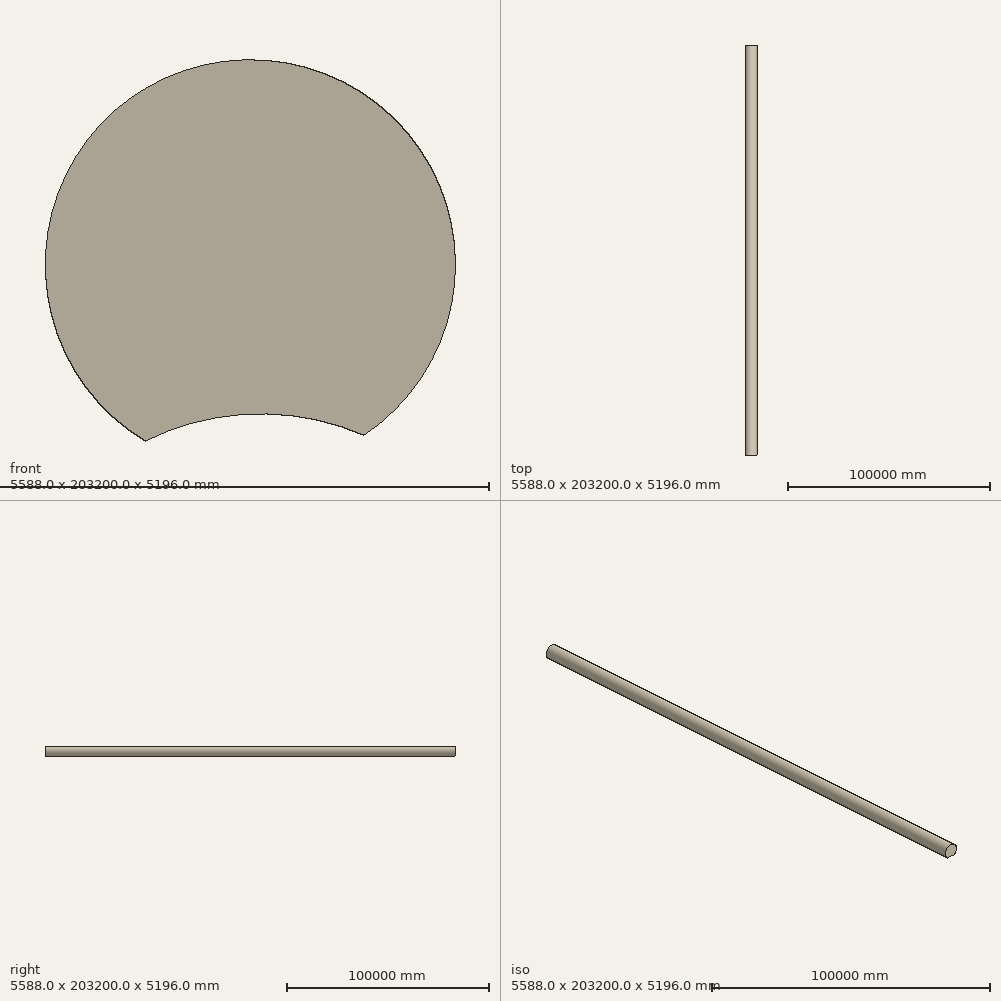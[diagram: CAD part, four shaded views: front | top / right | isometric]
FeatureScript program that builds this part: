
annotation { "Feature Type Name" : "Feature", "Feature Type Description" : "" }
export const myFeature = defineFeature(function(context is Context, id is Id, definition is map)
    precondition{}
    {
        {
            var Q0;
            Q0=qCreatedBy(makeId("Front.planeOp"),FACE);
            var sketch = newSketch(context, id + "F0", { "sketchPlane" : qUnion([Q0])});
            skArc(sketch, "E0", {"start": v(1550.8, -2324.1) * mm, "mid": v(-73.07, 2793.04) * mm, "end": v(-1427.15, -2402.02) * mm});
            skArc(sketch, "E1", {"start": v(1550.8, -2324.1) * mm, "mid": v(53.14, -2031.3) * mm, "end": v(-1427.15, -2402.02) * mm});
            skSolve(sketch);
        }
        {
            var Q0;
            Q0=makeQuery(id+"F0.imprint","IMPRINT",FACE,{"disambiguationData":[TD([[makeQuery(id+"F0.imprint","IMPRINT",EDGE,{"derivedFrom":sQuery(id+"F0.wireOp",EDGE,"E0")}),1.0]])]});
            extrude(context, id + "F1", {"entities" : qUnion([Q0]), "depth" : 203200 * mm});
        }
    });
